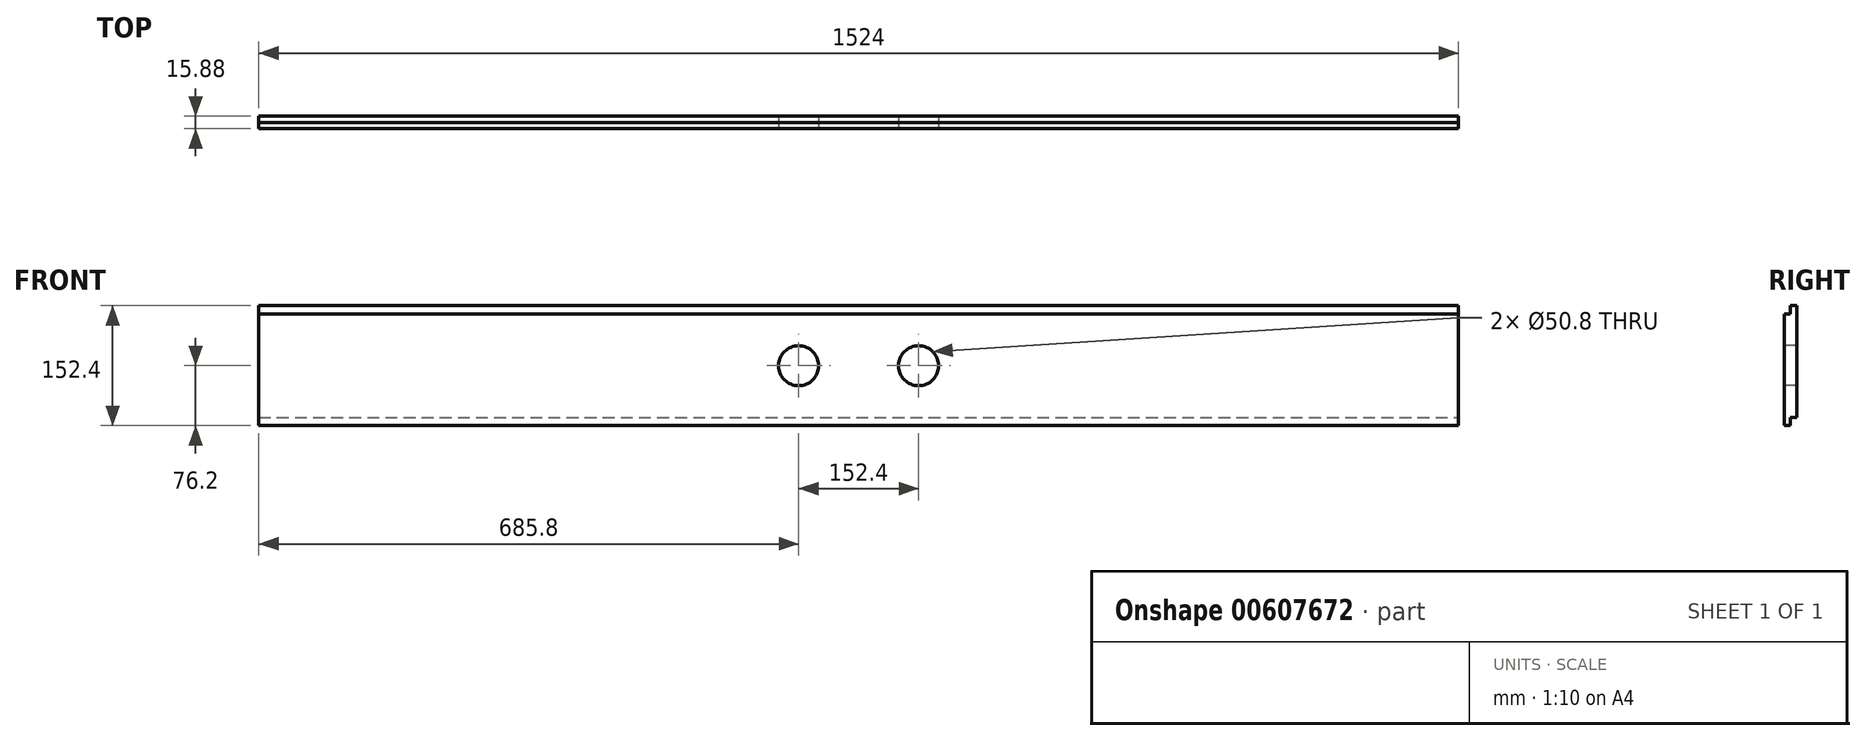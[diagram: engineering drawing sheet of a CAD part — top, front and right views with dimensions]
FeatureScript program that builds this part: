
annotation { "Feature Type Name" : "Feature", "Feature Type Description" : "" }
export const myFeature = defineFeature(function(context is Context, id is Id, definition is map)
    precondition{}
    {
        {
            var Q0;
            Q0=qCreatedBy(makeId("Front.planeOp"),FACE);
            var sketch = newSketch(context, id + "F0", { "sketchPlane" : qUnion([Q0])});
            skLineSegment(sketch, "E0", {"start": v(0, 0) * mm, "end": v(762, 0) * mm});
            skLineSegment(sketch, "E1", {"start": v(762, 0) * mm, "end": v(762, 76.2) * mm});
            skLineSegment(sketch, "E2.bottom", {"start": v(762, 76.2) * mm, "end": v(-762, 76.2) * mm});
            skLineSegment(sketch, "E2.top", {"start": v(762, -76.2) * mm, "end": v(-762, -76.2) * mm});
            skLineSegment(sketch, "E2.left", {"start": v(762, 76.2) * mm, "end": v(762, -76.2) * mm});
            skLineSegment(sketch, "E2.right", {"start": v(-762, 76.2) * mm, "end": v(-762, -76.2) * mm});
            skPoint(sketch, "E2.middle", {"position": v(0, 0) * mm});
            skSolve(sketch);
        }
        {
            var Q0;
            Q0=qSketchRegion(id+"F0",true);
            extrude(context, id + "F1", {"entities" : qUnion([Q0]), "depth" : 15.88 * mm, "offsetDistance" : 25.4 * mm});
        }
        {
            var Q0;
            Q0=makeQuery(id+"F1.opExtrude","SWEPT_FACE",FACE,{"disambiguationData":[OSD([sQuery(id+"F0.wireOp",EDGE,"E2.left")])]});
            var sketch = newSketch(context, id + "F2", { "sketchPlane" : qUnion([Q0])});
            skLineSegment(sketch, "E3", {"start": v(0, 76.2) * mm, "end": v(-7.87, 76.2) * mm});
            skLineSegment(sketch, "E4", {"start": v(-7.87, 76.2) * mm, "end": v(-7.87, 65.79) * mm});
            skLineSegment(sketch, "E5.bottom", {"start": v(-15.88, 76.2) * mm, "end": v(-7.87, 76.2) * mm});
            skLineSegment(sketch, "E5.top", {"start": v(-15.88, 65.79) * mm, "end": v(-7.87, 65.79) * mm});
            skLineSegment(sketch, "E5.left", {"start": v(-15.88, 76.2) * mm, "end": v(-15.88, 65.79) * mm});
            skLineSegment(sketch, "E6", {"start": v(-15.88, -76.2) * mm, "end": v(-8, -76.2) * mm});
            skLineSegment(sketch, "E7", {"start": v(-8, -76.2) * mm, "end": v(-8, -65.79) * mm});
            skLineSegment(sketch, "E8.bottom", {"start": v(0, -76.2) * mm, "end": v(-8, -76.2) * mm});
            skLineSegment(sketch, "E8.top", {"start": v(0, -65.79) * mm, "end": v(-8, -65.79) * mm});
            skLineSegment(sketch, "E8.left", {"start": v(0, -76.2) * mm, "end": v(0, -65.79) * mm});
            skSolve(sketch);
        }
        {
            var Q0;
            Q0=makeQuery(id+"F2.imprint","IMPRINT",FACE,{"disambiguationData":[TD([[makeQuery(id+"F2.imprint","IMPRINT",EDGE,{"derivedFrom":sQuery(id+"F2.wireOp",EDGE,"E8.bottom")}),1.0]])]});
            var Q1;
            Q1=makeQuery(id+"F2.imprint","IMPRINT",FACE,{"disambiguationData":[TD([[makeQuery(id+"F2.imprint","IMPRINT",EDGE,{"derivedFrom":sQuery(id+"F2.wireOp",EDGE,"E5.bottom")}),-1.0]])]});
            extrude(context, id + "F3", {"entities" : qUnion([Q0, Q1]), "operationType" : NewBodyOperationType.REMOVE, "endBound" : BoundingType.UP_TO_NEXT, "oppositeDirection" : true, "depth" : 25.4 * mm, "offsetDistance" : 25.4 * mm});
        }
        {
            var Q0;
            Q0=makeQuery(id+"F1.opExtrude","CAP_FACE",FACE,{"disambiguationData":[OSD([sQuery(id+"F0.wireOp",EDGE,"E2.bottom"),sQuery(id+"F0.wireOp",EDGE,"E2.top"),sQuery(id+"F0.wireOp",EDGE,"E2.left"),sQuery(id+"F0.wireOp",EDGE,"E2.right")])],"isStart":false});
            var sketch = newSketch(context, id + "F4", { "sketchPlane" : qUnion([Q0])});
            skLineSegment(sketch, "E9", {"start": v(0, 0) * mm, "end": v(76.2, 0) * mm});
            skLineSegment(sketch, "E10", {"start": v(0, 0) * mm, "end": v(-76.2, 0) * mm});
            skCircle(sketch, "E11", {"center": v(76.2, 0) * mm, "radius": 25.4 * mm});
            skCircle(sketch, "E12", {"center": v(-76.2, 0) * mm, "radius": 25.4 * mm});
            skSolve(sketch);
        }
        {
            var Q0;
            Q0 = qSketchRegion(id + "F4", true);
            extrude(context, id + "F5", {"entities" : qUnion([Q0]), "operationType" : NewBodyOperationType.REMOVE, "endBound" : BoundingType.UP_TO_NEXT, "oppositeDirection" : true, "depth" : 25.4 * mm, "offsetDistance" : 25.4 * mm});
        }
    });
